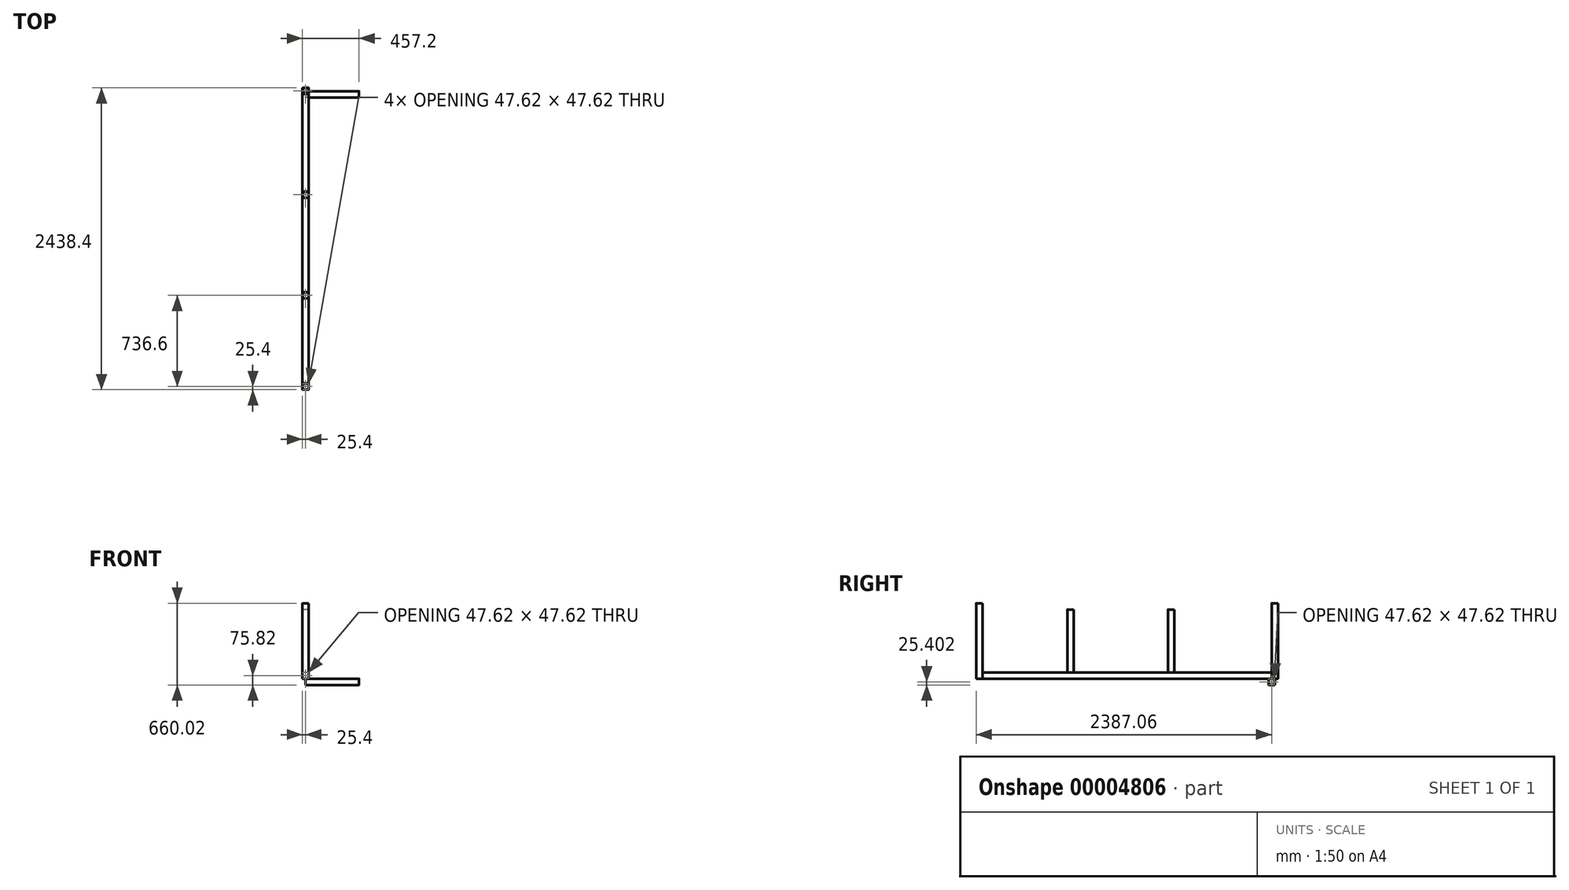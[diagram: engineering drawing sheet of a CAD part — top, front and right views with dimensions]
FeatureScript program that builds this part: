
annotation { "Feature Type Name" : "Feature", "Feature Type Description" : "" }
export const myFeature = defineFeature(function(context is Context, id is Id, definition is map)
    precondition{}
    {
        {
            var Q0;
            Q0=qCreatedBy(makeId("Front.planeOp"),FACE);
            var sketch = newSketch(context, id + "F0", { "sketchPlane" : qUnion([Q0])});
            skLineSegment(sketch, "E0.bottom", {"start": v(20.64, 49.21) * mm, "end": v(-20.64, 49.21) * mm});
            skLineSegment(sketch, "E0.top", {"start": v(20.64, 1.59) * mm, "end": v(-20.64, 1.59) * mm});
            skLineSegment(sketch, "E0.left", {"start": v(23.81, 46.04) * mm, "end": v(23.81, 4.76) * mm});
            skLineSegment(sketch, "E0.right", {"start": v(-23.81, 46.04) * mm, "end": v(-23.81, 4.76) * mm});
            skPoint(sketch, "E0.middle", {"position": v(0, 25.4) * mm});
            skPoint(sketch, "E1.visualSharp", {"position": v(-23.81, 49.21) * mm});
            skArc(sketch, "E1.filletArc", {"start": v(-20.64, 49.21) * mm, "mid": v(-22.88, 48.28) * mm, "end": v(-23.81, 46.04) * mm});
            skPoint(sketch, "E2.visualSharp", {"position": v(23.81, 49.21) * mm});
            skArc(sketch, "E2.filletArc", {"start": v(23.81, 46.04) * mm, "mid": v(22.88, 48.28) * mm, "end": v(20.64, 49.21) * mm});
            skPoint(sketch, "E3.visualSharp", {"position": v(23.81, 1.59) * mm});
            skArc(sketch, "E3.filletArc", {"start": v(20.64, 1.59) * mm, "mid": v(22.88, 2.52) * mm, "end": v(23.81, 4.76) * mm});
            skPoint(sketch, "E4.visualSharp", {"position": v(-23.81, 1.59) * mm});
            skArc(sketch, "E4.filletArc", {"start": v(-23.81, 4.76) * mm, "mid": v(-22.88, 2.52) * mm, "end": v(-20.64, 1.59) * mm});
            skLineSegment(sketch, "E5.bottom", {"start": v(23.81, 50.8) * mm, "end": v(-23.81, 50.8) * mm});
            skLineSegment(sketch, "E5.top", {"start": v(23.81, 0) * mm, "end": v(-23.81, 0) * mm});
            skLineSegment(sketch, "E5.left", {"start": v(25.4, 49.21) * mm, "end": v(25.4, 1.59) * mm});
            skLineSegment(sketch, "E5.right", {"start": v(-25.4, 49.21) * mm, "end": v(-25.4, 1.59) * mm});
            skPoint(sketch, "E6.visualSharp", {"position": v(-25.4, 50.8) * mm});
            skArc(sketch, "E6.filletArc", {"start": v(-23.81, 50.8) * mm, "mid": v(-24.94, 50.34) * mm, "end": v(-25.4, 49.21) * mm});
            skPoint(sketch, "E7.visualSharp", {"position": v(25.4, 50.8) * mm});
            skArc(sketch, "E7.filletArc", {"start": v(25.4, 49.21) * mm, "mid": v(24.94, 50.34) * mm, "end": v(23.81, 50.8) * mm});
            skPoint(sketch, "E8.visualSharp", {"position": v(25.4, 0) * mm});
            skArc(sketch, "E8.filletArc", {"start": v(23.81, 0) * mm, "mid": v(24.94, 0.46) * mm, "end": v(25.4, 1.59) * mm});
            skPoint(sketch, "E9.visualSharp", {"position": v(-25.4, 0) * mm});
            skArc(sketch, "E9.filletArc", {"start": v(-25.4, 1.59) * mm, "mid": v(-24.94, 0.46) * mm, "end": v(-23.81, 0) * mm});
            skSolve(sketch);
        }
        {
            var Q0;
            Q0=makeQuery(id+"F0.imprint","IMPRINT",FACE,{"disambiguationData":[TD([[makeQuery(id+"F0.imprint","IMPRINT",EDGE,{"derivedFrom":sQuery(id+"F0.wireOp",EDGE,"E0.bottom")}),-1.0]])]});
            extrude(context, id + "F1", {"entities" : qUnion([Q0]), "depth" : 2336.8 * mm});
        }
        {
            var Q0;
            Q0=makeQuery(id+"F1.opExtrude","SWEPT_FACE",FACE,{"disambiguationData":[OSD([sQuery(id+"F0.wireOp",EDGE,"E5.bottom")])]});
            var sketch = newSketch(context, id + "F2", { "sketchPlane" : qUnion([Q0])});
            skLineSegment(sketch, "E10.bottom", {"start": v(20.64, -788.99) * mm, "end": v(-20.64, -788.99) * mm});
            skLineSegment(sketch, "E10.top", {"start": v(20.64, -836.61) * mm, "end": v(-20.64, -836.61) * mm});
            skLineSegment(sketch, "E10.left", {"start": v(23.81, -792.16) * mm, "end": v(23.81, -833.44) * mm});
            skLineSegment(sketch, "E10.right", {"start": v(-23.81, -792.16) * mm, "end": v(-23.81, -833.44) * mm});
            skPoint(sketch, "E10.middle", {"position": v(0, -812.8) * mm});
            skPoint(sketch, "E11.visualSharp", {"position": v(-23.81, -788.99) * mm});
            skArc(sketch, "E11.filletArc", {"start": v(-20.64, -788.99) * mm, "mid": v(-22.88, -789.92) * mm, "end": v(-23.81, -792.16) * mm});
            skPoint(sketch, "E12.visualSharp", {"position": v(23.81, -788.99) * mm});
            skArc(sketch, "E12.filletArc", {"start": v(23.81, -792.16) * mm, "mid": v(22.88, -789.92) * mm, "end": v(20.64, -788.99) * mm});
            skPoint(sketch, "E13.visualSharp", {"position": v(23.81, -836.61) * mm});
            skArc(sketch, "E13.filletArc", {"start": v(20.64, -836.61) * mm, "mid": v(22.88, -835.68) * mm, "end": v(23.81, -833.44) * mm});
            skPoint(sketch, "E14.visualSharp", {"position": v(-23.81, -836.61) * mm});
            skArc(sketch, "E14.filletArc", {"start": v(-23.81, -833.44) * mm, "mid": v(-22.88, -835.68) * mm, "end": v(-20.64, -836.61) * mm});
            skLineSegment(sketch, "E15.bottom", {"start": v(23.81, -787.4) * mm, "end": v(-23.81, -787.4) * mm});
            skLineSegment(sketch, "E15.top", {"start": v(23.81, -838.2) * mm, "end": v(-23.81, -838.2) * mm});
            skLineSegment(sketch, "E15.left", {"start": v(25.4, -788.99) * mm, "end": v(25.4, -836.61) * mm});
            skLineSegment(sketch, "E15.right", {"start": v(-25.4, -788.99) * mm, "end": v(-25.4, -836.61) * mm});
            skPoint(sketch, "E16.visualSharp", {"position": v(-25.4, -787.4) * mm});
            skArc(sketch, "E16.filletArc", {"start": v(-23.81, -787.4) * mm, "mid": v(-24.94, -787.86) * mm, "end": v(-25.4, -788.99) * mm});
            skPoint(sketch, "E17.visualSharp", {"position": v(25.4, -787.4) * mm});
            skArc(sketch, "E17.filletArc", {"start": v(25.4, -788.99) * mm, "mid": v(24.94, -787.86) * mm, "end": v(23.81, -787.4) * mm});
            skPoint(sketch, "E18.visualSharp", {"position": v(25.4, -838.2) * mm});
            skArc(sketch, "E18.filletArc", {"start": v(23.81, -838.2) * mm, "mid": v(24.94, -837.74) * mm, "end": v(25.4, -836.61) * mm});
            skPoint(sketch, "E19.visualSharp", {"position": v(-25.4, -838.2) * mm});
            skArc(sketch, "E19.filletArc", {"start": v(-25.4, -836.61) * mm, "mid": v(-24.94, -837.74) * mm, "end": v(-23.81, -838.2) * mm});
            skLineSegment(sketch, "E20", {"start": v(-23.81, 0) * mm, "end": v(23.81, 0) * mm});
            skLineSegment(sketch, "E21.bottom", {"start": v(20.64, -1601.79) * mm, "end": v(-20.64, -1601.79) * mm});
            skLineSegment(sketch, "E21.top", {"start": v(20.64, -1649.41) * mm, "end": v(-20.64, -1649.41) * mm});
            skLineSegment(sketch, "E21.left", {"start": v(23.81, -1604.96) * mm, "end": v(23.81, -1646.24) * mm});
            skLineSegment(sketch, "E21.right", {"start": v(-23.81, -1604.96) * mm, "end": v(-23.81, -1646.24) * mm});
            skPoint(sketch, "E21.middle", {"position": v(0, -1625.6) * mm});
            skPoint(sketch, "E22.visualSharp", {"position": v(-23.81, -1601.79) * mm});
            skArc(sketch, "E22.filletArc", {"start": v(-20.64, -1601.79) * mm, "mid": v(-22.88, -1602.72) * mm, "end": v(-23.81, -1604.96) * mm});
            skPoint(sketch, "E23.visualSharp", {"position": v(23.81, -1601.79) * mm});
            skArc(sketch, "E23.filletArc", {"start": v(23.81, -1604.96) * mm, "mid": v(22.88, -1602.72) * mm, "end": v(20.64, -1601.79) * mm});
            skPoint(sketch, "E24.visualSharp", {"position": v(23.81, -1649.41) * mm});
            skArc(sketch, "E24.filletArc", {"start": v(20.64, -1649.41) * mm, "mid": v(22.88, -1648.48) * mm, "end": v(23.81, -1646.24) * mm});
            skPoint(sketch, "E25.visualSharp", {"position": v(-23.81, -1649.41) * mm});
            skArc(sketch, "E25.filletArc", {"start": v(-23.81, -1646.24) * mm, "mid": v(-22.88, -1648.48) * mm, "end": v(-20.64, -1649.41) * mm});
            skLineSegment(sketch, "E26.bottom", {"start": v(23.81, -1600.2) * mm, "end": v(-23.81, -1600.2) * mm});
            skLineSegment(sketch, "E26.top", {"start": v(23.81, -1651) * mm, "end": v(-23.81, -1651) * mm});
            skLineSegment(sketch, "E26.left", {"start": v(25.4, -1601.79) * mm, "end": v(25.4, -1649.41) * mm});
            skLineSegment(sketch, "E26.right", {"start": v(-25.4, -1601.79) * mm, "end": v(-25.4, -1649.41) * mm});
            skPoint(sketch, "E27.visualSharp", {"position": v(-25.4, -1600.2) * mm});
            skArc(sketch, "E27.filletArc", {"start": v(-23.81, -1600.2) * mm, "mid": v(-24.94, -1600.66) * mm, "end": v(-25.4, -1601.79) * mm});
            skPoint(sketch, "E28.visualSharp", {"position": v(25.4, -1600.2) * mm});
            skArc(sketch, "E28.filletArc", {"start": v(25.4, -1601.79) * mm, "mid": v(24.94, -1600.66) * mm, "end": v(23.81, -1600.2) * mm});
            skPoint(sketch, "E29.visualSharp", {"position": v(25.4, -1651) * mm});
            skArc(sketch, "E29.filletArc", {"start": v(23.81, -1651) * mm, "mid": v(24.94, -1650.54) * mm, "end": v(25.4, -1649.41) * mm});
            skPoint(sketch, "E30.visualSharp", {"position": v(-25.4, -1651) * mm});
            skArc(sketch, "E30.filletArc", {"start": v(-25.4, -1649.41) * mm, "mid": v(-24.94, -1650.54) * mm, "end": v(-23.81, -1651) * mm});
            skSolve(sketch);
        }
        {
            var Q0;
            Q0 = qSketchRegion(id + "F2", true);
            extrude(context, id + "F3", {"entities" : qUnion([Q0]), "depth" : 508 * mm});
        }
        {
            var Q0;
            Q0=qCreatedBy(makeId("Top.planeOp"),FACE);
            var sketch = newSketch(context, id + "F4", { "sketchPlane" : qUnion([Q0])});
            skLineSegment(sketch, "E31.bottom", {"start": v(20.64, 49.21) * mm, "end": v(-20.64, 49.21) * mm});
            skLineSegment(sketch, "E31.top", {"start": v(20.64, 1.59) * mm, "end": v(-20.64, 1.59) * mm});
            skLineSegment(sketch, "E31.left", {"start": v(23.81, 46.04) * mm, "end": v(23.81, 4.76) * mm});
            skLineSegment(sketch, "E31.right", {"start": v(-23.81, 46.04) * mm, "end": v(-23.81, 4.76) * mm});
            skPoint(sketch, "E31.middle", {"position": v(0, 25.4) * mm});
            skPoint(sketch, "E32.visualSharp", {"position": v(-23.81, 49.21) * mm});
            skArc(sketch, "E32.filletArc", {"start": v(-20.64, 49.21) * mm, "mid": v(-22.88, 48.28) * mm, "end": v(-23.81, 46.04) * mm});
            skPoint(sketch, "E33.visualSharp", {"position": v(23.81, 49.21) * mm});
            skArc(sketch, "E33.filletArc", {"start": v(23.81, 46.04) * mm, "mid": v(22.88, 48.28) * mm, "end": v(20.64, 49.21) * mm});
            skPoint(sketch, "E34.visualSharp", {"position": v(23.81, 1.59) * mm});
            skArc(sketch, "E34.filletArc", {"start": v(20.64, 1.59) * mm, "mid": v(22.88, 2.52) * mm, "end": v(23.81, 4.76) * mm});
            skPoint(sketch, "E35.visualSharp", {"position": v(-23.81, 1.59) * mm});
            skArc(sketch, "E35.filletArc", {"start": v(-23.81, 4.76) * mm, "mid": v(-22.88, 2.52) * mm, "end": v(-20.64, 1.59) * mm});
            skLineSegment(sketch, "E36.bottom", {"start": v(23.81, 50.8) * mm, "end": v(-23.81, 50.8) * mm});
            skLineSegment(sketch, "E36.top", {"start": v(23.81, 0) * mm, "end": v(-23.81, 0) * mm});
            skLineSegment(sketch, "E36.left", {"start": v(25.4, 49.21) * mm, "end": v(25.4, 1.59) * mm});
            skLineSegment(sketch, "E36.right", {"start": v(-25.4, 49.21) * mm, "end": v(-25.4, 1.59) * mm});
            skPoint(sketch, "E37.visualSharp", {"position": v(-25.4, 50.8) * mm});
            skArc(sketch, "E37.filletArc", {"start": v(-23.81, 50.8) * mm, "mid": v(-24.94, 50.34) * mm, "end": v(-25.4, 49.21) * mm});
            skPoint(sketch, "E38.visualSharp", {"position": v(25.4, 50.8) * mm});
            skArc(sketch, "E38.filletArc", {"start": v(25.4, 49.21) * mm, "mid": v(24.94, 50.34) * mm, "end": v(23.81, 50.8) * mm});
            skPoint(sketch, "E39.visualSharp", {"position": v(25.4, 0) * mm});
            skArc(sketch, "E39.filletArc", {"start": v(23.81, 0) * mm, "mid": v(24.94, 0.46) * mm, "end": v(25.4, 1.59) * mm});
            skPoint(sketch, "E40.visualSharp", {"position": v(-25.4, 0) * mm});
            skArc(sketch, "E40.filletArc", {"start": v(-25.4, 1.59) * mm, "mid": v(-24.94, 0.46) * mm, "end": v(-23.81, 0) * mm});
            skLineSegment(sketch, "E41.bottom", {"start": v(20.64, -2338.39) * mm, "end": v(-20.64, -2338.39) * mm});
            skLineSegment(sketch, "E41.top", {"start": v(20.64, -2386.01) * mm, "end": v(-20.64, -2386.01) * mm});
            skLineSegment(sketch, "E41.left", {"start": v(23.81, -2341.56) * mm, "end": v(23.81, -2382.84) * mm});
            skLineSegment(sketch, "E41.right", {"start": v(-23.81, -2341.56) * mm, "end": v(-23.81, -2382.84) * mm});
            skPoint(sketch, "E41.middle", {"position": v(0, -2362.2) * mm});
            skPoint(sketch, "E42.visualSharp", {"position": v(-23.81, -2338.39) * mm});
            skArc(sketch, "E42.filletArc", {"start": v(-20.64, -2338.39) * mm, "mid": v(-22.88, -2339.32) * mm, "end": v(-23.81, -2341.56) * mm});
            skPoint(sketch, "E43.visualSharp", {"position": v(23.81, -2338.39) * mm});
            skArc(sketch, "E43.filletArc", {"start": v(23.81, -2341.56) * mm, "mid": v(22.88, -2339.32) * mm, "end": v(20.64, -2338.39) * mm});
            skPoint(sketch, "E44.visualSharp", {"position": v(23.81, -2386.01) * mm});
            skArc(sketch, "E44.filletArc", {"start": v(20.64, -2386.01) * mm, "mid": v(22.88, -2385.08) * mm, "end": v(23.81, -2382.84) * mm});
            skPoint(sketch, "E45.visualSharp", {"position": v(-23.81, -2386.01) * mm});
            skArc(sketch, "E45.filletArc", {"start": v(-23.81, -2382.84) * mm, "mid": v(-22.88, -2385.08) * mm, "end": v(-20.64, -2386.01) * mm});
            skLineSegment(sketch, "E46.bottom", {"start": v(23.81, -2336.8) * mm, "end": v(-23.81, -2336.8) * mm});
            skLineSegment(sketch, "E46.top", {"start": v(23.81, -2387.6) * mm, "end": v(-23.81, -2387.6) * mm});
            skLineSegment(sketch, "E46.left", {"start": v(25.4, -2338.39) * mm, "end": v(25.4, -2386.01) * mm});
            skLineSegment(sketch, "E46.right", {"start": v(-25.4, -2338.39) * mm, "end": v(-25.4, -2386.01) * mm});
            skPoint(sketch, "E47.visualSharp", {"position": v(-25.4, -2336.8) * mm});
            skArc(sketch, "E47.filletArc", {"start": v(-23.81, -2336.8) * mm, "mid": v(-24.94, -2337.26) * mm, "end": v(-25.4, -2338.39) * mm});
            skPoint(sketch, "E48.visualSharp", {"position": v(25.4, -2336.8) * mm});
            skArc(sketch, "E48.filletArc", {"start": v(25.4, -2338.39) * mm, "mid": v(24.94, -2337.26) * mm, "end": v(23.81, -2336.8) * mm});
            skPoint(sketch, "E49.visualSharp", {"position": v(25.4, -2387.6) * mm});
            skArc(sketch, "E49.filletArc", {"start": v(23.81, -2387.6) * mm, "mid": v(24.94, -2387.14) * mm, "end": v(25.4, -2386.01) * mm});
            skPoint(sketch, "E50.visualSharp", {"position": v(-25.4, -2387.6) * mm});
            skArc(sketch, "E50.filletArc", {"start": v(-25.4, -2386.01) * mm, "mid": v(-24.94, -2387.14) * mm, "end": v(-23.81, -2387.6) * mm});
            skSolve(sketch);
        }
        {
            var Q0;
            Q0 = qSketchRegion(id + "F4", true);
            extrude(context, id + "F5", {"entities" : qUnion([Q0]), "depth" : 609.6 * mm});
        }
        {
            var Q0;
            Q0=qCreatedBy(makeId("Right.planeOp"),FACE);
            var sketch = newSketch(context, id + "F6", { "sketchPlane" : qUnion([Q0])});
            skLineSegment(sketch, "E51.bottom", {"start": v(20.1, -1.2) * mm, "end": v(-21.18, -1.2) * mm});
            skLineSegment(sketch, "E51.top", {"start": v(20.1, -48.83) * mm, "end": v(-21.18, -48.83) * mm});
            skLineSegment(sketch, "E51.left", {"start": v(23.27, -4.38) * mm, "end": v(23.27, -45.66) * mm});
            skLineSegment(sketch, "E51.right", {"start": v(-24.35, -4.38) * mm, "end": v(-24.35, -45.66) * mm});
            skPoint(sketch, "E51.middle", {"position": v(-0.54, -25.02) * mm});
            skPoint(sketch, "E52.visualSharp", {"position": v(-24.35, -1.2) * mm});
            skArc(sketch, "E52.filletArc", {"start": v(-21.18, -1.2) * mm, "mid": v(-23.42, -2.14) * mm, "end": v(-24.35, -4.38) * mm});
            skPoint(sketch, "E53.visualSharp", {"position": v(23.27, -1.2) * mm});
            skArc(sketch, "E53.filletArc", {"start": v(23.27, -4.38) * mm, "mid": v(22.34, -2.14) * mm, "end": v(20.1, -1.2) * mm});
            skPoint(sketch, "E54.visualSharp", {"position": v(23.27, -48.83) * mm});
            skArc(sketch, "E54.filletArc", {"start": v(20.1, -48.83) * mm, "mid": v(22.34, -47.9) * mm, "end": v(23.27, -45.66) * mm});
            skPoint(sketch, "E55.visualSharp", {"position": v(-24.35, -48.83) * mm});
            skArc(sketch, "E55.filletArc", {"start": v(-24.35, -45.66) * mm, "mid": v(-23.42, -47.9) * mm, "end": v(-21.18, -48.83) * mm});
            skLineSegment(sketch, "E56.bottom", {"start": v(23.27, 0.38) * mm, "end": v(-24.35, 0.38) * mm});
            skLineSegment(sketch, "E56.top", {"start": v(23.27, -50.42) * mm, "end": v(-24.35, -50.42) * mm});
            skLineSegment(sketch, "E56.left", {"start": v(24.86, -1.2) * mm, "end": v(24.86, -48.83) * mm});
            skLineSegment(sketch, "E56.right", {"start": v(-25.94, -1.2) * mm, "end": v(-25.94, -48.83) * mm});
            skPoint(sketch, "E57.visualSharp", {"position": v(-25.94, 0.38) * mm});
            skArc(sketch, "E57.filletArc", {"start": v(-24.35, 0.38) * mm, "mid": v(-25.47, -0.08) * mm, "end": v(-25.94, -1.2) * mm});
            skPoint(sketch, "E58.visualSharp", {"position": v(24.86, 0.38) * mm});
            skArc(sketch, "E58.filletArc", {"start": v(24.86, -1.2) * mm, "mid": v(24.4, -0.08) * mm, "end": v(23.27, 0.38) * mm});
            skPoint(sketch, "E59.visualSharp", {"position": v(24.86, -50.42) * mm});
            skArc(sketch, "E59.filletArc", {"start": v(23.27, -50.42) * mm, "mid": v(24.4, -49.95) * mm, "end": v(24.86, -48.83) * mm});
            skPoint(sketch, "E60.visualSharp", {"position": v(-25.94, -50.42) * mm});
            skArc(sketch, "E60.filletArc", {"start": v(-25.94, -48.83) * mm, "mid": v(-25.47, -49.95) * mm, "end": v(-24.35, -50.42) * mm});
            skSolve(sketch);
        }
        {
            var Q0;
            Q0 = qSketchRegion(id + "F6", true);
            extrude(context, id + "F7", {"entities" : qUnion([Q0]), "depth" : 431.8 * mm});
        }
    });
